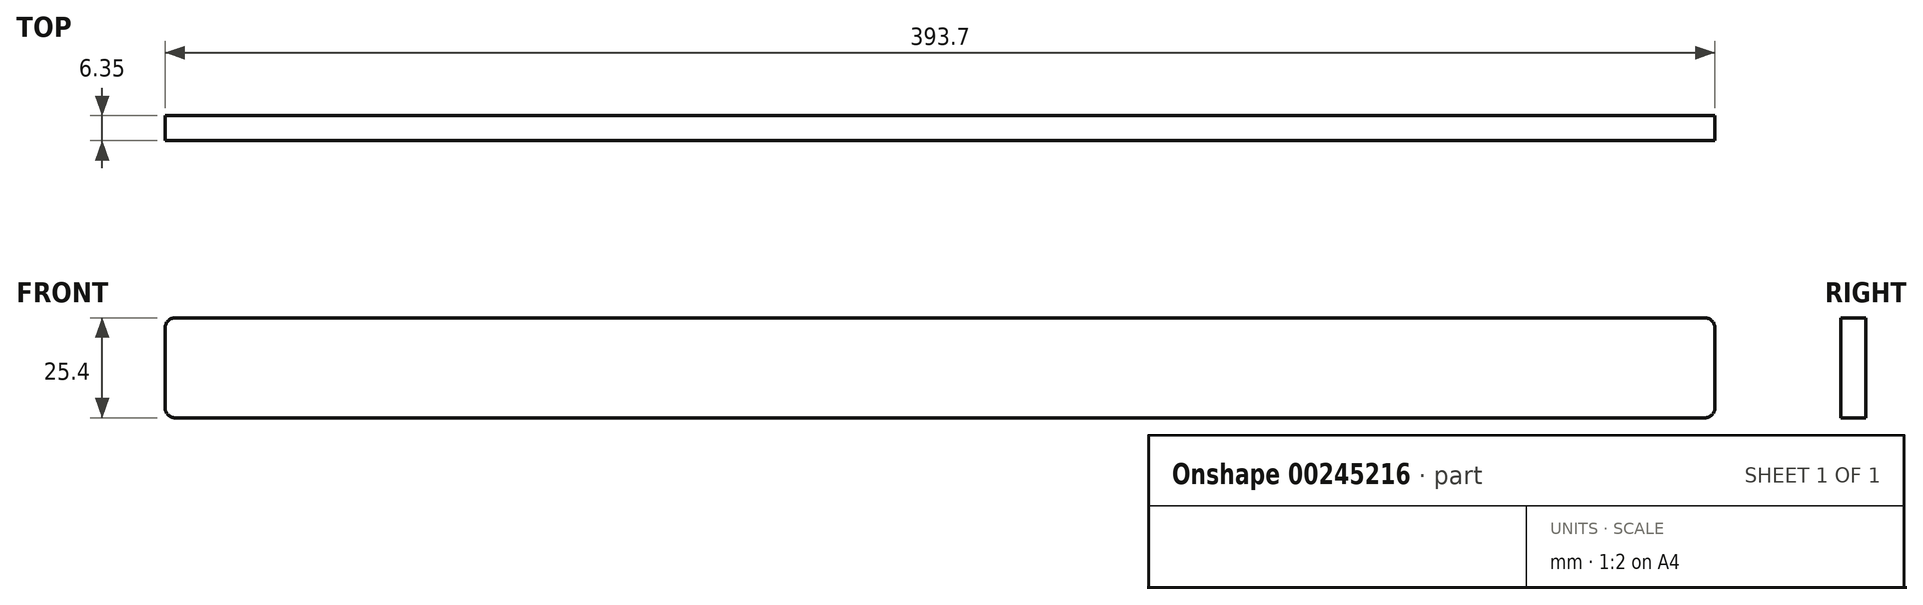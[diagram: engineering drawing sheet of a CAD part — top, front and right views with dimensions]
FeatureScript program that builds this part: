
annotation { "Feature Type Name" : "Feature", "Feature Type Description" : "" }
export const myFeature = defineFeature(function(context is Context, id is Id, definition is map)
    precondition{}
    {
        {
            var Q0;
            Q0=qCreatedBy(makeId("Front.planeOp"),FACE);
            var sketch = newSketch(context, id + "F0", { "sketchPlane" : qUnion([Q0])});
            skLineSegment(sketch, "E0.bottom", {"start": v(-194.31, 12.7) * mm, "end": v(194.31, 12.7) * mm});
            skLineSegment(sketch, "E0.top", {"start": v(-194.31, -12.7) * mm, "end": v(194.31, -12.7) * mm});
            skLineSegment(sketch, "E0.left", {"start": v(-196.85, 10.16) * mm, "end": v(-196.85, -10.16) * mm});
            skLineSegment(sketch, "E0.right", {"start": v(196.85, 10.16) * mm, "end": v(196.85, -10.16) * mm});
            skPoint(sketch, "E0.middle", {"position": v(0, 0) * mm});
            skPoint(sketch, "E1.visualSharp", {"position": v(-196.85, 12.7) * mm});
            skArc(sketch, "E1.filletArc", {"start": v(-194.31, 12.7) * mm, "mid": v(-196.1, 11.96) * mm, "end": v(-196.85, 10.16) * mm});
            skPoint(sketch, "E2.visualSharp", {"position": v(-196.85, -12.7) * mm});
            skArc(sketch, "E2.filletArc", {"start": v(-196.85, -10.16) * mm, "mid": v(-196.1, -11.96) * mm, "end": v(-194.31, -12.7) * mm});
            skPoint(sketch, "E3.visualSharp", {"position": v(196.85, 12.7) * mm});
            skArc(sketch, "E3.filletArc", {"start": v(196.85, 10.16) * mm, "mid": v(196.1, 11.96) * mm, "end": v(194.31, 12.7) * mm});
            skPoint(sketch, "E4.visualSharp", {"position": v(196.85, -12.7) * mm});
            skArc(sketch, "E4.filletArc", {"start": v(194.31, -12.7) * mm, "mid": v(196.1, -11.96) * mm, "end": v(196.85, -10.16) * mm});
            skSolve(sketch);
        }
        {
            var Q0;
            Q0 = qSketchRegion(id + "F0", true);
            extrude(context, id + "F1", {"entities" : qUnion([Q0]), "depth" : 6.35 * mm});
        }
    });
